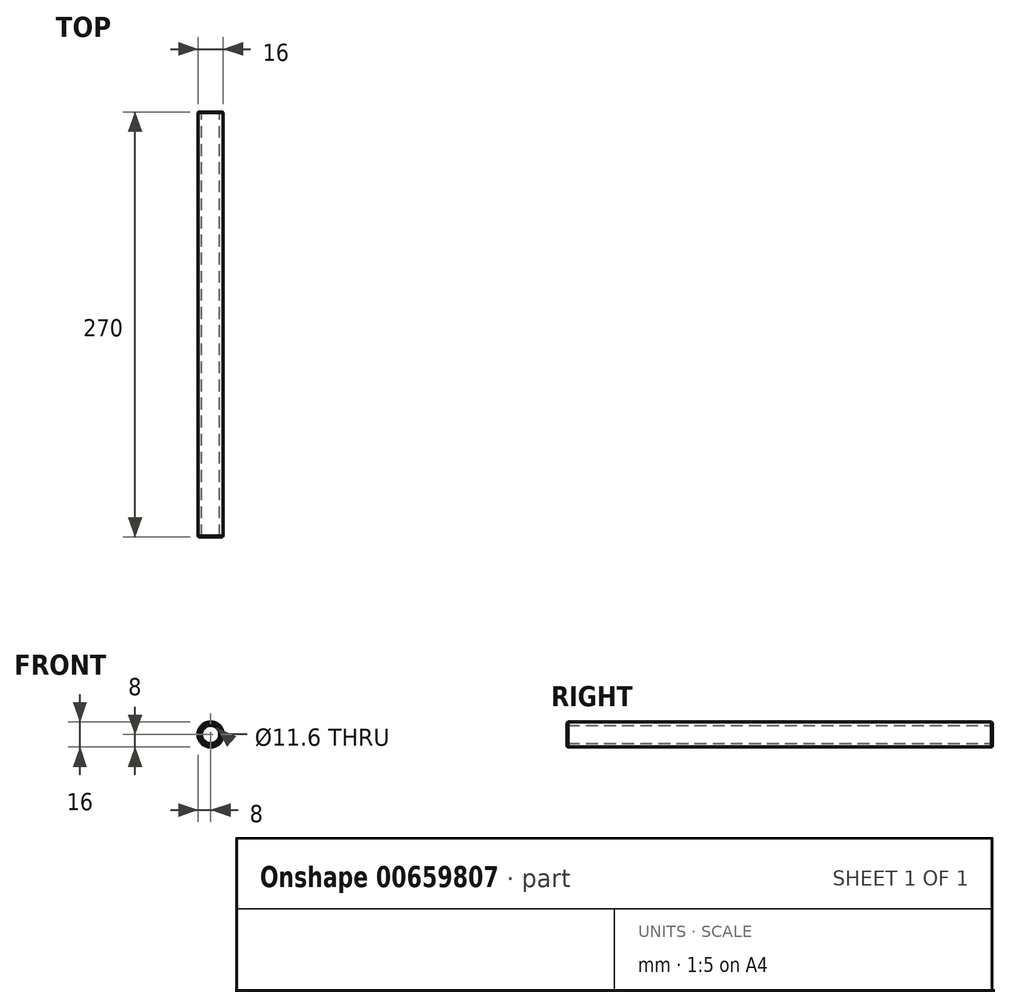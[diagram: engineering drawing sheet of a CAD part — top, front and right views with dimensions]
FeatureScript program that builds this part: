
annotation { "Feature Type Name" : "Feature", "Feature Type Description" : "" }
export const myFeature = defineFeature(function(context is Context, id is Id, definition is map)
    precondition{}
    {
        {
            var Q0;
            Q0=qCreatedBy(makeId("Front.planeOp"),FACE);
            var sketch = newSketch(context, id + "F0", { "sketchPlane" : qUnion([Q0])});
            skCircle(sketch, "E0", {"center": v(0, 0) * mm, "radius": 8 * mm});
            skCircle(sketch, "E1", {"center": v(0, 0) * mm, "radius": 5.8 * mm});
            skSolve(sketch);
        }
        {
            var Q0;
            Q0=makeQuery(id+"F0.imprint","IMPRINT",FACE,{"disambiguationData":[TD([[makeQuery(id+"F0.imprint","IMPRINT",EDGE,{"derivedFrom":sQuery(id+"F0.wireOp",EDGE,"E0")}),1.0]])]});
            extrude(context, id + "F1", {"entities" : qUnion([Q0]), "depth" : 270 * mm, "offsetDistance" : 25 * mm});
        }
        {
            var Q0;
            Q0=makeQuery(id+"F1.opExtrude","CAP_EDGE",EDGE,{"disambiguationData":[OSD([sQuery(id+"F0.wireOp",EDGE,"E1")])],"isStart":false});
            var Q1;
            Q1=makeQuery(id+"F1.opExtrude","CAP_EDGE",EDGE,{"disambiguationData":[OSD([sQuery(id+"F0.wireOp",EDGE,"E0")])],"isStart":false});
            var Q2;
            Q2=makeQuery(id+"F1.opExtrude","CAP_EDGE",EDGE,{"disambiguationData":[OSD([sQuery(id+"F0.wireOp",EDGE,"E1")])],"isStart":true});
            var Q3;
            Q3=makeQuery(id+"F1.opExtrude","CAP_EDGE",EDGE,{"disambiguationData":[OSD([sQuery(id+"F0.wireOp",EDGE,"E0")])],"isStart":true});
            chamfer(context, id + "F2", {"entities" : qUnion([Q0, Q1, Q2, Q3]), "width" : 0.5 * mm, "tangentPropagation" : true});
        }
    });
